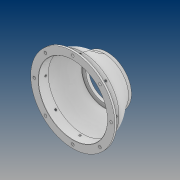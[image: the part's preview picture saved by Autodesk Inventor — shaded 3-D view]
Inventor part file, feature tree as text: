
AUTODESK INVENTOR PART (.ipt)
format: ipt  version: 2021 (Build 250183000, 183)  size: 377,856 bytes
history: native  units: mm
features: thread x10, sketch x7, extrude x5, pattern_circular x4, revolve x3, fillet x3, plane x1
ambient origin geometry x8: Origin, YZ Plane, XZ Plane, XY Plane, X Axis, Y Axis, Z Axis, Center Point
bodies: Solid1 (feature_tree)
feature tree (33):
  sketch  "Sketch1"  dims[d0=930.0mm d1=762.0mm]
  extrude  "Extrusion1"  Depth=762.0mm
  extrude  "Extrusion2"  TaperAngle=0.0deg  [1 undecoded]
  pattern_circular  "Circular Pattern1"  Count=2  [1 undecoded]
  extrude  "Extrusion3"  Depth=80.0mm TaperAngle=360.0deg
  sketch  "Sketch3"  dims[d4=425.0mm d5=20.0mm d6=0.0mm]
  revolve  "Revolution6"  [1 undecoded]
  plane  "Work Plane2"
  revolve  "Revolution7"  Angle=90.0deg
  extrude  "Extrusion7"  TaperAngle=90.0deg  [1 undecoded]
  pattern_circular  "Circular Pattern5"  [2 undecoded]
  revolve  "Revolution8"  [1 undecoded]
  pattern_circular  "Circular Pattern6"  [2 undecoded]
  extrude  "Extrusion8"  Depth=3.0mm TaperAngle=360.0deg
  pattern_circular  "Circular Pattern7"  Angle=90.0deg  [1 undecoded]
  thread  "Thread13"  [1 undecoded]
  thread  "Thread14"  [1 undecoded]
  thread  "Thread15"  [1 undecoded]
  thread  "Thread16"  [1 undecoded]
  thread  "Thread17"  [1 undecoded]
  thread  "Thread18"  [1 undecoded]
  thread  "Thread19"  [1 undecoded]
  thread  "Thread20"  [1 undecoded]
  thread  "Thread21"  [1 undecoded]
  thread  "Thread22"  [1 undecoded]
  fillet  "Fillet4"  Radius=15.0mm
  fillet  "Fillet5"  Radius=15.0mm
  fillet  "Fillet6"  Radius=15.0mm
  sketch  "Sketch2"  dims[d2=30.0mm d3=0.0mm]
  sketch  "Sketch8"  dims[d7=20.0mm d8=0.0mm d9=80.0mm d10=360.0deg]
  sketch  "Sketch13"  dims[d12=762.0mm d13=802.0mm]
  sketch  "Sketch14"  dims[d14=90.0mm d15=0.0mm d58=90.0deg]
  sketch  "Sketch15"  dims[d99=360.278mm d107=90.0deg d108=465.0mm d109=25.0mm d110=15.0mm d111=0.0mm d112=60.0mm d113=360.0deg d115=90.0deg d116=60.0mm d117=360.0deg d119=21.0mm d120=0.0mm d121=60.0mm d122=0.0mm d123=0.0mm d124=80.0mm d125=360.0deg d127=20.145mm d128=0.0mm d129=20.145mm d130=0.0mm d131=20.145mm d132=0.0mm d133=20.145mm d134=0.0mm d135=15.0mm d136=0.0mm d137=15.0mm d138=0.0mm d139=15.0mm d140=0.0mm d141=15.0mm d142=0.0mm d143=15.0mm d144=0.0mm d145=15.0mm d146=0.0mm d147=3.0mm d148=3.0mm d149=3.0mm d100=0.872665mm d101=0.5mm d102=0.872665mm]
note: 20 required parameter values undecoded (feature->parameter linkage not recoverable at this tier; creation-order binding heuristic only, values carry confidence <= 0.55)